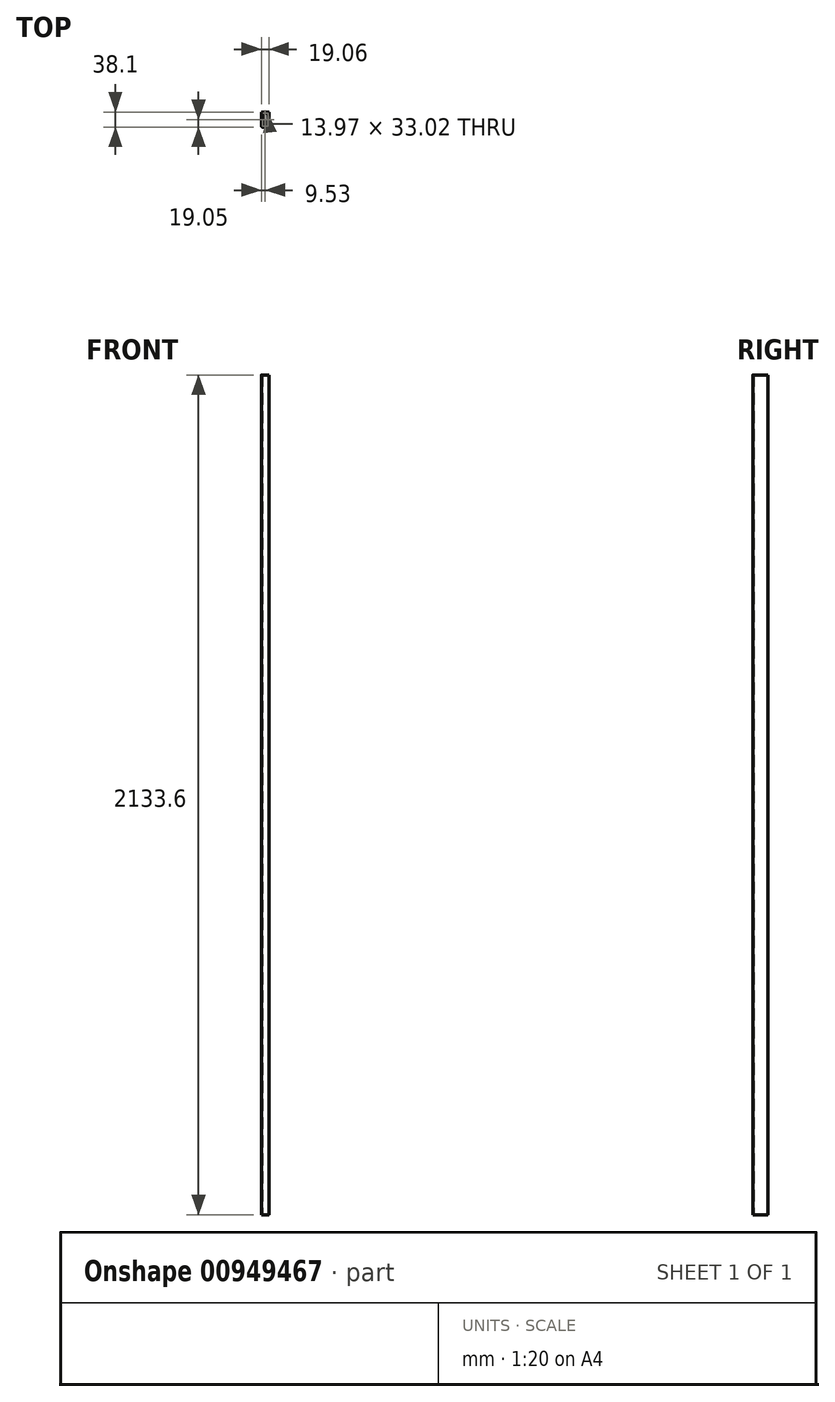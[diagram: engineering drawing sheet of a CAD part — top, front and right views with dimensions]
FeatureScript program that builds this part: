
annotation { "Feature Type Name" : "Feature", "Feature Type Description" : "" }
export const myFeature = defineFeature(function(context is Context, id is Id, definition is map)
    precondition{}
    {
        {
            var Q0;
            Q0=qCreatedBy(makeId("Top.planeOp"),FACE);
            var sketch = newSketch(context, id + "F0", { "sketchPlane" : qUnion([Q0])});
            skLineSegment(sketch, "E0.bottom", {"start": v(-8.02, 19.05) * mm, "end": v(8.03, 19.05) * mm});
            skLineSegment(sketch, "E0.top", {"start": v(-8.02, -19.05) * mm, "end": v(8.03, -19.05) * mm});
            skLineSegment(sketch, "E0.left", {"start": v(-9.53, 17.55) * mm, "end": v(-9.53, -17.55) * mm});
            skLineSegment(sketch, "E0.right", {"start": v(9.53, 17.55) * mm, "end": v(9.52, -17.55) * mm});
            skPoint(sketch, "E0.middle", {"position": v(0, 0) * mm});
            skPoint(sketch, "E1.visualSharp", {"position": v(-9.52, 19.05) * mm});
            skArc(sketch, "E1.filletArc", {"start": v(-8.02, 19.05) * mm, "mid": v(-9.09, 18.61) * mm, "end": v(-9.52, 17.55) * mm});
            skPoint(sketch, "E2.visualSharp", {"position": v(9.53, 19.05) * mm});
            skArc(sketch, "E2.filletArc", {"start": v(9.53, 17.55) * mm, "mid": v(9.09, 18.61) * mm, "end": v(8.03, 19.05) * mm});
            skPoint(sketch, "E3.visualSharp", {"position": v(9.52, -19.05) * mm});
            skArc(sketch, "E3.filletArc", {"start": v(8.03, -19.05) * mm, "mid": v(9.09, -18.61) * mm, "end": v(9.53, -17.55) * mm});
            skPoint(sketch, "E4.visualSharp", {"position": v(-9.53, -19.05) * mm});
            skArc(sketch, "E4.filletArc", {"start": v(-9.52, -17.55) * mm, "mid": v(-9.09, -18.61) * mm, "end": v(-8.02, -19.05) * mm});
            skLineSegment(sketch, "E5.0", {"start": v(-6.98, 16.5) * mm, "end": v(6.99, 16.5) * mm});
            skLineSegment(sketch, "E5.1", {"start": v(-6.98, 16.5) * mm, "end": v(-6.99, -16.51) * mm});
            skLineSegment(sketch, "E5.2", {"start": v(-6.99, -16.51) * mm, "end": v(6.98, -16.51) * mm});
            skLineSegment(sketch, "E5.3", {"start": v(6.99, 16.5) * mm, "end": v(6.98, -16.51) * mm});
            skSolve(sketch);
        }
        {
            var Q0;
            Q0=makeQuery(id+"F0.imprint","IMPRINT",FACE,{"disambiguationData":[TD([[makeQuery(id+"F0.imprint","IMPRINT",EDGE,{"derivedFrom":sQuery(id+"F0.wireOp",EDGE,"E0.bottom")}),-1.0]])]});
            extrude(context, id + "F1", {"entities" : qUnion([Q0]), "offsetDistance" : 25.4 * mm, "depth" : 2133.6 * mm});
        }
    });
